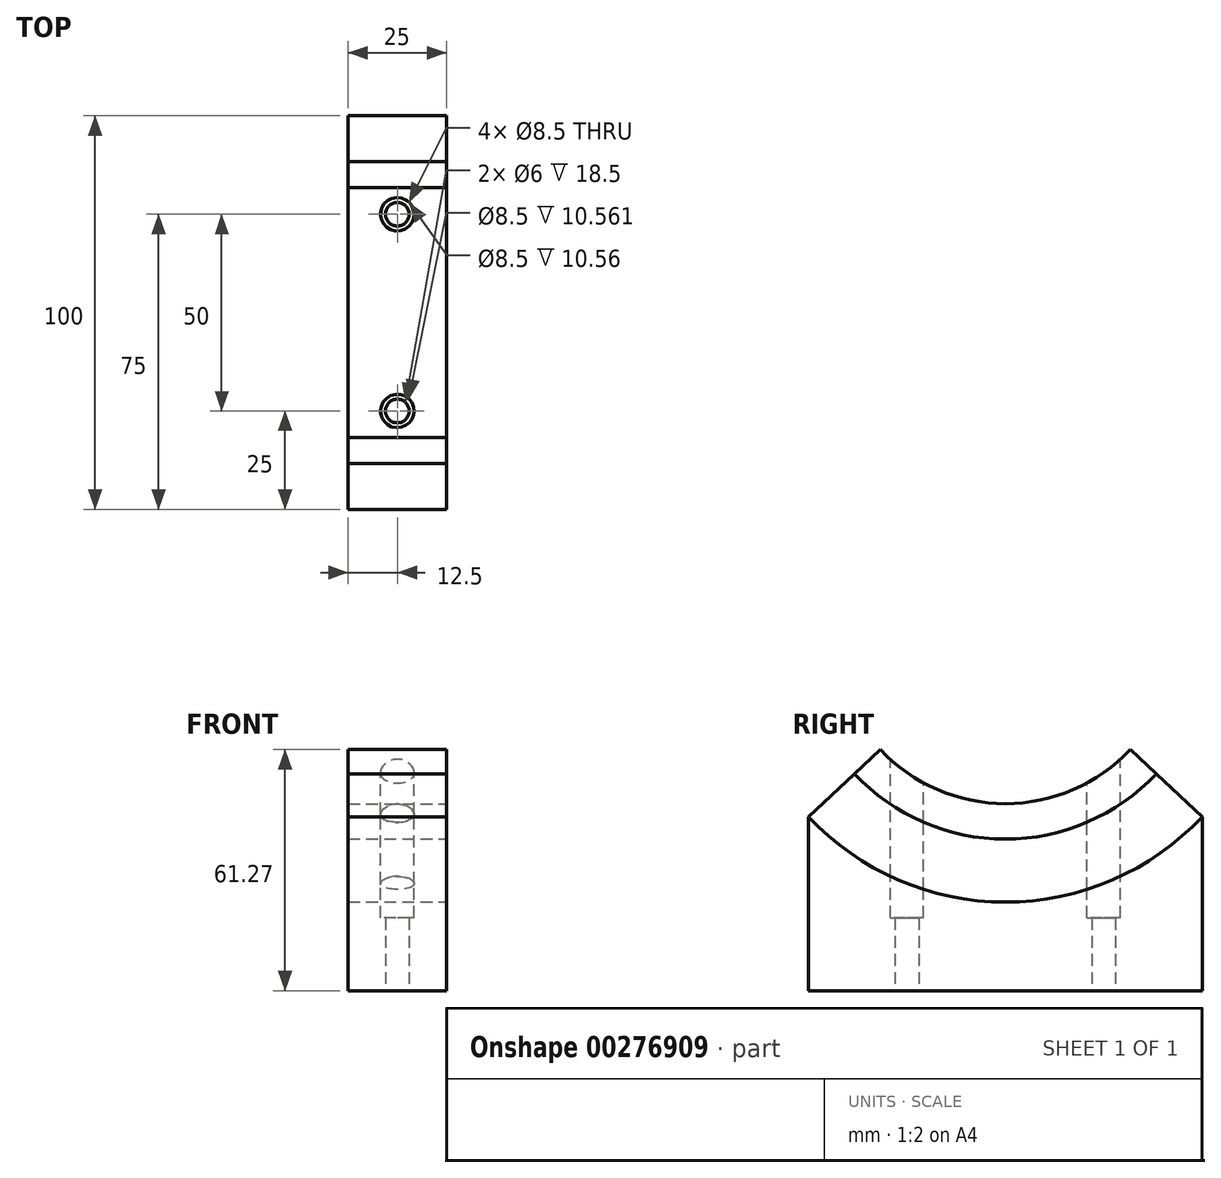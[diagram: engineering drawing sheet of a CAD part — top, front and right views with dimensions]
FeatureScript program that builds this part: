
annotation { "Feature Type Name" : "Feature", "Feature Type Description" : "" }
export const myFeature = defineFeature(function(context is Context, id is Id, definition is map)
    precondition{}
    {
        {
            var Q0;
            Q0=qCreatedBy(makeId("Top.planeOp"),FACE);
            var sketch = newSketch(context, id + "F0", { "sketchPlane" : qUnion([Q0])});
            skLineSegment(sketch, "E0.0", {"start": v(12.5, 50) * mm, "end": v(-12.5, 50) * mm, "construction": true});
            skLineSegment(sketch, "E1.0", {"start": v(12.5, -50) * mm, "end": v(-12.5, -50) * mm, "construction": true});
            skLineSegment(sketch, "E2", {"start": v(0, 50) * mm, "end": v(0, -50) * mm, "construction": true});
            skLineSegment(sketch, "E3", {"start": v(0, 0) * mm, "end": v(-20.03, 0) * mm, "construction": true});
            skPoint(sketch, "E3.endSnap0", {"position": v(0, 0) * mm});
            skCircle(sketch, "E4", {"center": v(0, -25) * mm, "radius": 3 * mm});
            skCircle(sketch, "E5", {"center": v(0, 25) * mm, "radius": 3 * mm});
            skSolve(sketch);
        }
        {
            var Q0;
            Q0=sQuery(id+"F0.wireOp",VERTEX,"E0.0.start");
            var Q1;
            Q1=qCreatedBy(makeId("Right.planeOp"),FACE);
            cPlane(context, id + "F1", {"entities" : qUnion([Q0, Q1]), "cplaneType" : CPlaneType.PLANE_POINT, "offset" : 25 * mm, "width" : 150 * mm, "height" : 150 * mm});
        }
        {
            var Q0;
            Q0=qCreatedBy(id+"F1.planeOp",FACE);
            var sketch = newSketch(context, id + "F2", { "sketchPlane" : qUnion([Q0])});
            skCircle(sketch, "E6.0", {"center": v(0, 91) * mm, "radius": 10 * mm, "construction": true});
            skLineSegment(sketch, "E7.0", {"start": v(75, 0) * mm, "end": v(-75, 0) * mm});
            skLineSegment(sketch, "E8", {"start": v(0, 91) * mm, "end": v(0, 0) * mm, "construction": true});
            skCircle(sketch, "E9", {"center": v(0, 91) * mm, "radius": 68.5 * mm});
            skLineSegment(sketch, "E10", {"start": v(0, 91) * mm, "end": v(50, 44.18) * mm});
            skLineSegment(sketch, "E11", {"start": v(50, 44.18) * mm, "end": v(50, 0) * mm});
            skLineSegment(sketch, "E12", {"start": v(-50, 44.18) * mm, "end": v(-50, 0) * mm});
            skCircle(sketch, "E13", {"center": v(0, 91) * mm, "radius": 52.5 * mm});
            skLineSegment(sketch, "E14", {"start": v(0, 91) * mm, "end": v(-50, 44.18) * mm});
            skCircle(sketch, "E15", {"center": v(0, 91) * mm, "radius": 43.5 * mm});
            skLineSegment(sketch, "E16", {"start": v(-25.17, 0) * mm, "end": v(-25.17, 55.52) * mm, "construction": true});
            skLineSegment(sketch, "E17", {"start": v(-25.17, 44.93) * mm, "end": v(-37.37, 44.93) * mm, "construction": true});
            skSolve(sketch);
        }
        {
            var Q0;
            {var subQ0=sQuery(id+"F2.wireOp",EDGE,"E11");Q0=makeQuery(id+"F2.imprint","IMPRINT",FACE,{"disambiguationData":[TD([[makeQuery(id+"F2.imprint","IMPRINT",EDGE,{"derivedFrom":subQ0}),-1.0]])]});}
            extrude(context, id + "F3", {"entities" : qUnion([Q0]), "oppositeDirection" : true, "depth" : 25 * mm});
        }
        {
            var Q0;
            {var subQ0=sQuery(id+"F2.wireOp",EDGE,"E10");var subQ5=sQuery(id+"F2.wireOp",EDGE,"E13");var subQ6=makeQuery(id+"F2.imprint","INTERSECT",VERTEX,{"derivedFrom":[subQ0,subQ5]});Q0=makeQuery(id+"F2.imprint","IMPRINT",FACE,{"disambiguationData":[TD([[makeQuery(id+"F2.imprint","IMPRINT",EDGE,{"disambiguationData":[TD([[subQ6,1.0]])],"derivedFrom":subQ5}),-1.0]])]});}
            extrude(context, id + "F4", {"entities" : qUnion([Q0]), "oppositeDirection" : true, "depth" : 25 * mm});
        }
        {
            var Q0;
            {var subQ0=sQuery(id+"F2.wireOp",EDGE,"E15");var subQ1=sQuery(id+"F2.wireOp",EDGE,"E10");var subQ2=makeQuery(id+"F2.imprint","INTERSECT",VERTEX,{"derivedFrom":[subQ1,subQ0]});Q0=makeQuery(id+"F2.imprint","IMPRINT",FACE,{"disambiguationData":[TD([[makeQuery(id+"F2.imprint","IMPRINT",EDGE,{"disambiguationData":[TD([[subQ2,-1.0]])],"derivedFrom":subQ1}),-1.0]])]});}
            extrude(context, id + "F5", {"entities" : qUnion([Q0]), "oppositeDirection" : true, "depth" : 25 * mm});
        }
        {
            var Q0;
            Q0=makeQuery(id+"F0.imprint","IMPRINT",FACE,{"disambiguationData":[TD([[makeQuery(id+"F0.imprint","IMPRINT",EDGE,{"derivedFrom":sQuery(id+"F0.wireOp",EDGE,"E4")}),1.0]])]});
            var Q1;
            Q1=makeQuery(id+"F0.imprint","IMPRINT",FACE,{"disambiguationData":[TD([[makeQuery(id+"F0.imprint","IMPRINT",EDGE,{"derivedFrom":sQuery(id+"F0.wireOp",EDGE,"E5")}),1.0]])]});
            extrude(context, id + "F6", {"entities" : qUnion([Q0, Q1]), "operationType" : NewBodyOperationType.REMOVE, "endBound" : BoundingType.THROUGH_ALL, "depth" : 25 * mm});
        }
        {
            var Q0;
            Q0=qCreatedBy(makeId("Top.planeOp"),FACE);
            cPlane(context, id + "F7", {"entities" : qUnion([Q0]), "cplaneType" : CPlaneType.OFFSET, "offset" : 70 * mm, "width" : 150 * mm, "height" : 150 * mm});
        }
        {
            var Q0;
            Q0=qCreatedBy(id+"F7.planeOp",FACE);
            var sketch = newSketch(context, id + "F8", { "sketchPlane" : qUnion([Q0])});
            skCircle(sketch, "E18.0", {"center": v(0, -25) * mm, "radius": 3 * mm, "construction": true});
            skCircle(sketch, "E19", {"center": v(0, -25) * mm, "radius": 4.25 * mm});
            skCircle(sketch, "E20", {"center": v(0, 25) * mm, "radius": 4.25 * mm});
            skSolve(sketch);
        }
        {
            var Q0;
            Q0=makeQuery(id+"F8.imprint","IMPRINT",FACE,{"disambiguationData":[TD([[makeQuery(id+"F8.imprint","IMPRINT",EDGE,{"derivedFrom":sQuery(id+"F8.wireOp",EDGE,"E19")}),1.0]])]});
            var Q1;
            Q1=makeQuery(id+"F8.imprint","IMPRINT",FACE,{"disambiguationData":[TD([[makeQuery(id+"F8.imprint","IMPRINT",EDGE,{"derivedFrom":sQuery(id+"F8.wireOp",EDGE,"E20")}),1.0]])]});
            var Q2;
            Q2=sQuery(id+"F8.wireOp",EDGE,"E19");
            extrude(context, id + "F9", {"entities" : qUnion([Q0, Q1]), "operationType" : NewBodyOperationType.REMOVE, "surfaceEntities" : qUnion([Q2]), "oppositeDirection" : true, "depth" : 22.5 * mm});
        }
        {
            var Q0;
            Q0=makeQuery(id+"F8.imprint","IMPRINT",FACE,{"disambiguationData":[TD([[makeQuery(id+"F8.imprint","IMPRINT",EDGE,{"derivedFrom":sQuery(id+"F8.wireOp",EDGE,"E19")}),1.0]])]});
            var Q1;
            Q1=makeQuery(id+"F8.imprint","IMPRINT",FACE,{"disambiguationData":[TD([[makeQuery(id+"F8.imprint","IMPRINT",EDGE,{"derivedFrom":sQuery(id+"F8.wireOp",EDGE,"E20")}),1.0]])]});
            extrude(context, id + "F10", {"entities" : qUnion([Q0, Q1]), "operationType" : NewBodyOperationType.REMOVE, "oppositeDirection" : true, "depth" : 34 * mm});
        }
        {
            var Q0;
            Q0=makeQuery(id+"F8.imprint","IMPRINT",FACE,{"disambiguationData":[TD([[makeQuery(id+"F8.imprint","IMPRINT",EDGE,{"derivedFrom":sQuery(id+"F8.wireOp",EDGE,"E20")}),1.0]])]});
            var Q1;
            Q1=makeQuery(id+"F8.imprint","IMPRINT",FACE,{"disambiguationData":[TD([[makeQuery(id+"F8.imprint","IMPRINT",EDGE,{"derivedFrom":sQuery(id+"F8.wireOp",EDGE,"E19")}),1.0]])]});
            extrude(context, id + "F11", {"entities" : qUnion([Q0, Q1]), "operationType" : NewBodyOperationType.REMOVE, "oppositeDirection" : true, "depth" : 51.5 * mm});
        }
    });
